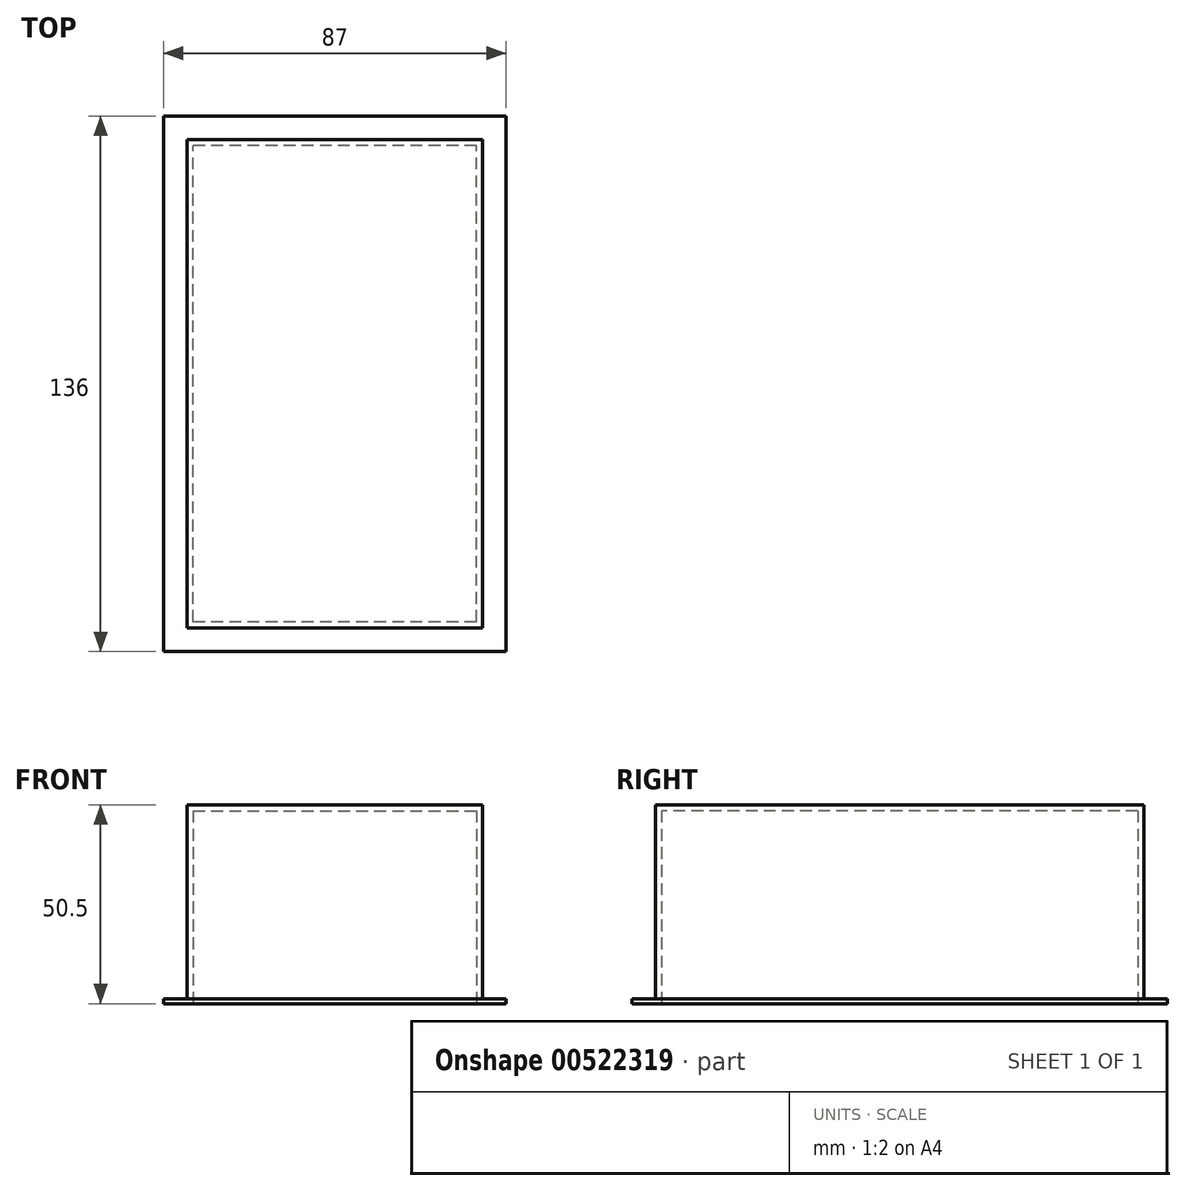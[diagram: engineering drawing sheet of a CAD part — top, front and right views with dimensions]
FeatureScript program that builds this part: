
annotation { "Feature Type Name" : "Feature", "Feature Type Description" : "" }
export const myFeature = defineFeature(function(context is Context, id is Id, definition is map)
    precondition{}
    {
        {
            var Q0;
            Q0=qCreatedBy(makeId("Top.planeOp"),FACE);
            var sketch = newSketch(context, id + "F0", { "sketchPlane" : qUnion([Q0])});
            skLineSegment(sketch, "E0.bottom", {"start": v(-48.95, 44.74) * mm, "end": v(26.05, 44.74) * mm});
            skLineSegment(sketch, "E0.top", {"start": v(-48.95, -79.26) * mm, "end": v(26.05, -79.26) * mm});
            skLineSegment(sketch, "E0.left", {"start": v(-48.95, 44.74) * mm, "end": v(-48.95, -79.26) * mm});
            skLineSegment(sketch, "E0.right", {"start": v(26.05, 44.74) * mm, "end": v(26.05, -79.26) * mm});
            skLineSegment(sketch, "E1.bottom", {"start": v(-54.95, 50.74) * mm, "end": v(32.05, 50.74) * mm});
            skLineSegment(sketch, "E1.top", {"start": v(-54.95, -85.26) * mm, "end": v(32.05, -85.26) * mm});
            skLineSegment(sketch, "E1.left", {"start": v(-54.95, 50.74) * mm, "end": v(-54.95, -85.26) * mm});
            skLineSegment(sketch, "E1.right", {"start": v(32.05, 50.74) * mm, "end": v(32.05, -85.26) * mm});
            skSolve(sketch);
        }
        {
            var Q0;
            Q0=makeQuery(id+"F0.imprint","IMPRINT",FACE,{"disambiguationData":[TD([[makeQuery(id+"F0.imprint","IMPRINT",EDGE,{"derivedFrom":sQuery(id+"F0.wireOp",EDGE,"E0.bottom")}),-1.0]])]});
            extrude(context, id + "F1", {"entities" : qUnion([Q0]), "depth" : 50.5 * mm, "offsetDistance" : 25 * mm});
        }
        {
            var Q0;
            Q0 = qSketchRegion(id + "F0", true);
            extrude(context, id + "F2", {"entities" : qUnion([Q0]), "operationType" : NewBodyOperationType.ADD, "depth" : 1.2 * mm, "offsetDistance" : 25 * mm});
        }
        {
            var Q0;
            {var subQ0=sQuery(id+"F0.wireOp",EDGE,"E0.right");var subQ1=sQuery(id+"F0.wireOp",EDGE,"E0.left");var subQ2=sQuery(id+"F0.wireOp",EDGE,"E0.top");var subQ3=sQuery(id+"F0.wireOp",EDGE,"E0.bottom");Q0=makeQuery(id+"F2.boolean.opBoolean","MERGE",FACE,{"derivedFrom":[makeQuery(id+"F1.opExtrude","CAP_FACE",FACE,{"disambiguationData":[OSD([subQ3,subQ2,subQ1,subQ0])],"isStart":true}),makeQuery(id+"F2.opExtrude","CAP_FACE",FACE,{"disambiguationData":[OSD([subQ3,subQ2,subQ1,subQ0,sQuery(id+"F0.wireOp",EDGE,"E1.bottom"),sQuery(id+"F0.wireOp",EDGE,"E1.top"),sQuery(id+"F0.wireOp",EDGE,"E1.left"),sQuery(id+"F0.wireOp",EDGE,"E1.right")])],"isStart":true})]});}
            shell(context, id + "F3", {"entities" : qUnion([Q0]), "thickness" : 1.5 * mm});
        }
    });
